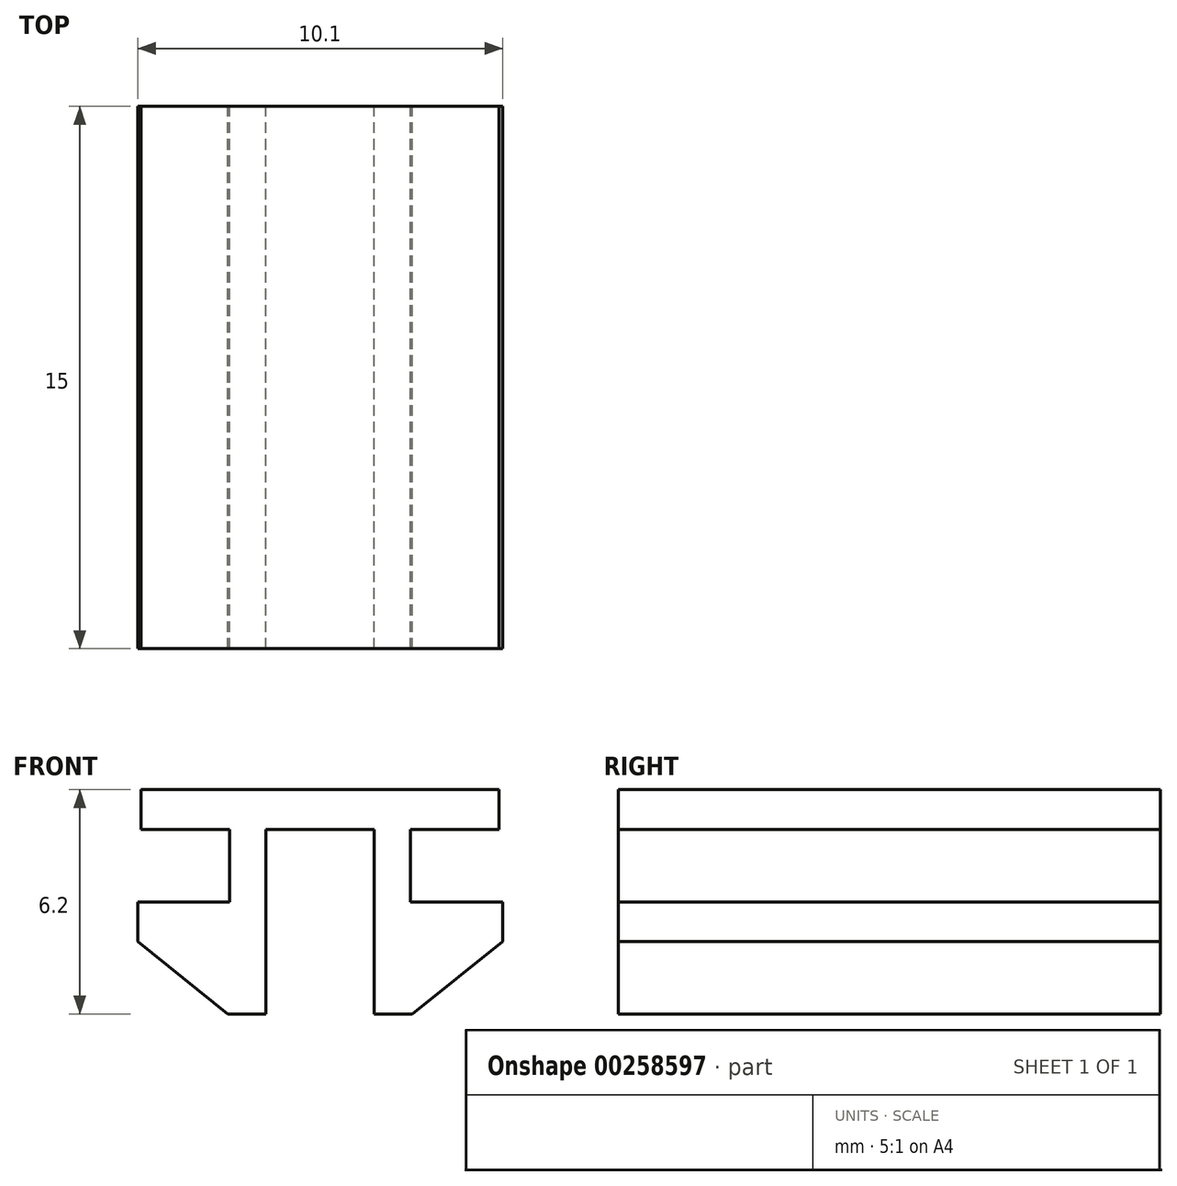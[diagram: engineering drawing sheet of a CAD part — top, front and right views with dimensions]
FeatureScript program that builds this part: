
annotation { "Feature Type Name" : "Feature", "Feature Type Description" : "" }
export const myFeature = defineFeature(function(context is Context, id is Id, definition is map)
    precondition{}
    {
        {
            var Q0;
            Q0=qCreatedBy(makeId("Front.planeOp"),FACE);
            var sketch = newSketch(context, id + "F0", { "sketchPlane" : qUnion([Q0])});
            skLineSegment(sketch, "E0.top", {"start": v(-5.05, 0.55) * mm, "end": v(-2.5, 0.55) * mm});
            skLineSegment(sketch, "E0.left", {"start": v(-5.05, -0.55) * mm, "end": v(-5.05, 0.55) * mm});
            skLineSegment(sketch, "E0.right", {"start": v(5.05, -0.55) * mm, "end": v(5.05, 0.55) * mm});
            skPoint(sketch, "E0.middle", {"position": v(0, 0) * mm});
            skLineSegment(sketch, "E1.top", {"start": v(-2.55, -2.55) * mm, "end": v(-1.5, -2.55) * mm});
            skLineSegment(sketch, "E2", {"start": v(-1.5, -2.55) * mm, "end": v(-2.55, -2.55) * mm});
            skLineSegment(sketch, "E3.MirrorCS", {"start": v(1.5, -2.55) * mm, "end": v(2.55, -2.55) * mm});
            skLineSegment(sketch, "E4", {"start": v(-2.55, -2.55) * mm, "end": v(-5.05, -0.55) * mm});
            skLineSegment(sketch, "E5", {"start": v(2.55, -2.55) * mm, "end": v(5.05, -0.55) * mm});
            skLineSegment(sketch, "E6", {"start": v(0, 0) * mm, "end": v(0, 2.55) * mm});
            skPoint(sketch, "E6.endSnap0", {"position": v(0, 0.55) * mm});
            skLineSegment(sketch, "E7.0", {"start": v(2.5, 0.55) * mm, "end": v(2.5, 2.55) * mm});
            skLineSegment(sketch, "E8.0", {"start": v(-2.5, 0.55) * mm, "end": v(-2.5, 2.55) * mm});
            skLineSegment(sketch, "E9.0", {"start": v(1.5, -2.55) * mm, "end": v(1.5, 2.55) * mm});
            skLineSegment(sketch, "E10.0", {"start": v(-1.5, -2.55) * mm, "end": v(-1.5, 2.55) * mm});
            skPoint(sketch, "E11.orphan", {"position": v(0, -2.55) * mm});
            skLineSegment(sketch, "E12.0", {"start": v(-4.95, 2.55) * mm, "end": v(-2.5, 2.55) * mm});
            skLineSegment(sketch, "E13.trimOffspring", {"start": v(2.5, 0.55) * mm, "end": v(5.05, 0.55) * mm});
            skLineSegment(sketch, "E14.top", {"start": v(-4.95, 3.65) * mm, "end": v(4.95, 3.65) * mm});
            skLineSegment(sketch, "E14.left", {"start": v(-4.95, 2.55) * mm, "end": v(-4.95, 3.65) * mm});
            skLineSegment(sketch, "E14.right", {"start": v(4.95, 2.55) * mm, "end": v(4.95, 3.65) * mm});
            skLineSegment(sketch, "E15.trimOffspring", {"start": v(-1.5, 2.55) * mm, "end": v(1.5, 2.55) * mm});
            skLineSegment(sketch, "E16.trimOffspring", {"start": v(2.5, 2.55) * mm, "end": v(4.95, 2.55) * mm});
            skSolve(sketch);
        }
        {
            var Q0;
            Q0=qSketchRegion(id+"F0",true);
            extrude(context, id + "F1", {"entities" : qUnion([Q0]), "depth" : 15 * mm});
        }
    });
